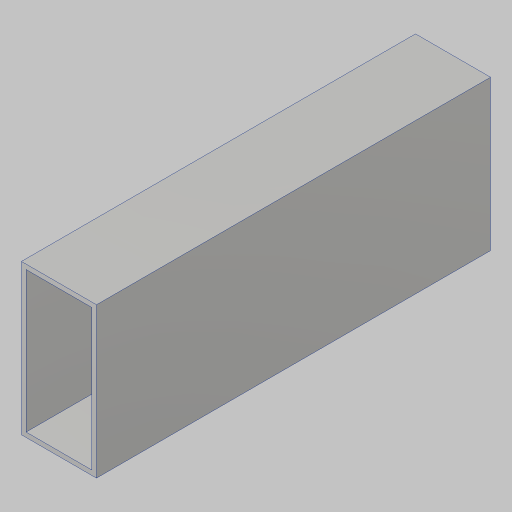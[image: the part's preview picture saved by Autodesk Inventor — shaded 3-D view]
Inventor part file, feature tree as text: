
AUTODESK INVENTOR PART (.ipt)
format: ipt  version: 2023.5 (Build 275446000, 446)  size: 205,824 bytes
history: native  units: in
note: dims shown in document units (in); Inventor stores cm internally (conversion verified against a paired STEP export)
features: extrude x1
ambient origin geometry x8: Origin, YZ Plane, XZ Plane, XY Plane, X Axis, Y Axis, Z Axis, Center Point
bodies: Solid1 (feature_tree)
feature tree (1):
  extrude  "Extrusion1"  TaperAngle=0.0deg  [1 undecoded]
note: 1 required parameter value undecoded (feature->parameter linkage not recoverable at this tier; creation-order binding heuristic only, values carry confidence <= 0.55)
